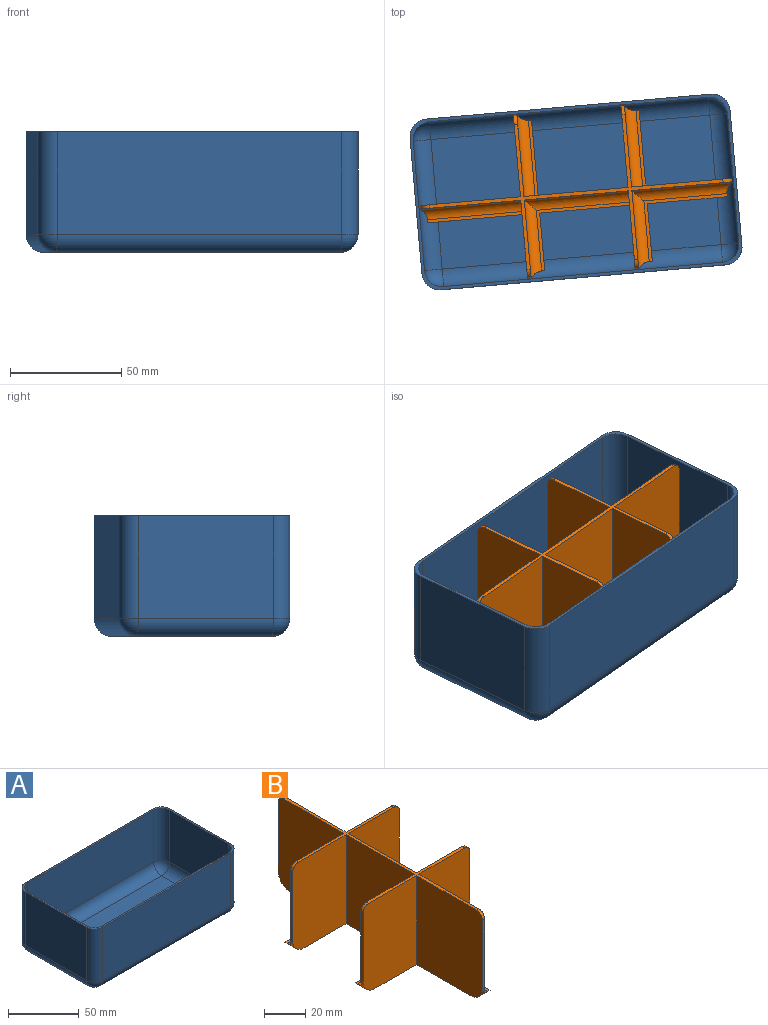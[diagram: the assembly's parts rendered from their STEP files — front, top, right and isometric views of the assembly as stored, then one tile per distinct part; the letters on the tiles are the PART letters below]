
ASSEMBLY  parts=2 mates=1
PART A: 35 faces, bbox 144.6x77.1x54.3 mm
  f0: plane 61.1x46.3mm, normal (1,0,0), area 2828.9mm2, adj f8,f13,f16,f26
  f1: plane 128.6x46.3mm, normal (0,1,0), area 5954.2mm2, adj f8,f13,f14,f22
  f2: plane 61.1x46.3mm, normal (-1,0,0), area 2828.9mm2, adj f8,f14,f15,f19
  f3: plane 58.5x45mm, normal (1,0,0), area 2632.5mm2, adj f8,f9,f12,f32
  f4: plane 126x45mm, normal (0,-1,0), area 5670mm2, adj f8,f9,f10,f28
  f5: plane 58.5x45mm, normal (-1,0,0), area 2632.5mm2, adj f8,f10,f11,f29
  f6: plane 126x45mm, normal (0,1,0), area 5670mm2, adj f8,f11,f12,f33
  f7: plane 128.6x46.3mm, normal (0,-1,0), area 5954.2mm2, adj f8,f15,f16,f23
  f8: plane 144.6x77.1mm, normal (0,0,1), area 569.7mm2, adj f0,f1,f2,f3,f4,f5,f6,f7
  f9: cylinder r=8mm len=45mm, axis (0,0,-1), area 565.5mm2, adj f3,f4,f8,f30
  f10: cylinder r=8mm len=45mm, axis (0,0,1), area 565.5mm2, adj f4,f5,f8,f27
  f11: cylinder r=8mm len=45mm, axis (0,0,-1), area 565.5mm2, adj f5,f6,f8,f31
  f12: cylinder r=8mm len=45mm, axis (0,0,1), area 565.5mm2, adj f3,f6,f8,f34
  f13: cylinder r=8mm len=46.3mm, axis (0,0,-1), area 581.8mm2, adj f0,f1,f8,f24
  f14: cylinder r=8mm len=46.3mm, axis (0,0,1), area 581.8mm2, adj f1,f2,f8,f20
  f15: cylinder r=8mm len=46.3mm, axis (0,0,-1), area 581.8mm2, adj f2,f7,f8,f21
  f16: cylinder r=8mm len=46.3mm, axis (0,0,1), area 581.8mm2, adj f0,f7,f8,f25
  f17: plane 126x58.5mm, normal (0,0,1), area 7371mm2, adj f28,f29,f32,f33
  f18: plane 128.6x61.1mm, normal (0,0,-1), area 7857.5mm2, adj f19,f22,f23,f26
  f19: cylinder r=8mm len=61.1mm, axis (0,-1,0), area 767.8mm2, adj f2,f18,f20,f21
  f20: sphere r=8mm, area 100.5mm2, adj f14,f19,f22
  f21: sphere r=8mm, area 100.5mm2, adj f15,f19,f23
  f22: cylinder r=8mm len=128.6mm, axis (-1,0,0), area 1616mm2, adj f1,f18,f20,f24
  f23: cylinder r=8mm len=128.6mm, axis (1,0,0), area 1616mm2, adj f7,f18,f21,f25
  f24: sphere r=8mm, area 100.5mm2, adj f13,f22,f26
  f25: sphere r=8mm, area 100.5mm2, adj f16,f23,f26
  f26: cylinder r=8mm len=61.1mm, axis (0,1,0), area 767.8mm2, adj f0,f18,f24,f25
  f27: sphere r=8mm, area 100.5mm2, adj f10,f28,f29
  f28: cylinder r=8mm len=126mm, axis (1,0,0), area 1583.4mm2, adj f4,f17,f27,f30
  f29: cylinder r=8mm len=58.5mm, axis (0,-1,0), area 735.1mm2, adj f5,f17,f27,f31
  f30: sphere r=8mm, area 100.5mm2, adj f9,f28,f32
  f31: sphere r=8mm, area 100.5mm2, adj f11,f29,f33
  f32: cylinder r=8mm len=58.5mm, axis (0,1,0), area 735.1mm2, adj f3,f17,f30,f34
  f33: cylinder r=8mm len=126mm, axis (-1,0,0), area 1583.4mm2, adj f6,f17,f31,f34
  f34: sphere r=8mm, area 100.5mm2, adj f12,f32,f33
PART B: 53 faces, bbox 73.5x140.7x53 mm
  f0: plane 40.6x2mm, normal (1,0,0), area 81.2mm2, adj f8,f11,f23,f30
  f1: plane 42.54x2mm, normal (1,0,0), area 81.8mm2, adj f2,f11,f32,f39
  f2: plane 42.54x1.4mm, normal (0,0,1), area 59.6mm2, adj f1,f32,f39,f40
  f3: plane 47x46mm, normal (1,0,0), area 2162mm2, adj f13,f23,f31,f43
  f4: plane 46x45.25mm, normal (1,0,0), area 2078mm2, adj f13,f14,f32,f39,f40,f52
  f5: plane 53x47mm, normal (-1,0,0), area 2472.8mm2, adj f11,f13,f20,f26,f27,f28,f45
  f6: plane 53x45.25mm, normal (-1,0,0), area 2381.1mm2, adj f11,f13,f14,f29,f39,f52
  f7: plane 36.14x2mm, normal (1,0,0), area 69mm2, adj f11,f12,f21,f38
  f8: plane 42x27.44mm, normal (0,0,1), area 95.3mm2, adj f0,f23,f30,f35,f43,f44
  f9: plane 46x45.25mm, normal (1,0,0), area 2078mm2, adj f13,f15,f22,f38,f41,f51
  f10: plane 53x45.25mm, normal (-1,0,0), area 2362.9mm2, adj f11,f13,f15,f17,f18,f19,f38,f46
  f11: plane 124.7x57.5mm, normal (0,0,-1), area 1789.6mm2, adj f0,f1,f5,f6,f7,f10,f19,f20
  f12: plane 37.54x27.44mm, normal (0,0,1), area 89mm2, adj f7,f21,f37,f38,f41,f42
  f13: plane 132.7x65.5mm, normal (0,0,1), area 416.8mm2, adj f3,f4,f5,f6,f9,f10,f17,f20
  f14: plane 41x1.6mm, normal (0,-1,0), area 65.6mm2, adj f4,f6,f39,f52
  f15: plane 41x1.6mm, normal (0,1,0), area 65.6mm2, adj f9,f10,f38,f51
  f16: plane 41x1.6mm, normal (-1,0,0), area 65.6mm2, adj f17,f20,f36,f49
  f17: plane 46x36.75mm, normal (0,1,0), area 1687mm2, adj f10,f13,f16,f36,f46,f49
  f18: plane 34.04x1.4mm, normal (0,0,1), area 47.7mm2, adj f10,f19,f36,f46
  f19: plane 34.04x2mm, normal (0,1,0), area 64.8mm2, adj f10,f11,f18,f36
  f20: plane 53x36.75mm, normal (0,-1,0), area 1930.6mm2, adj f5,f11,f13,f16,f36,f49
  f21: plane 26.04x2mm, normal (0,1,0), area 48.8mm2, adj f7,f11,f12,f37
  f22: plane 46x35.15mm, normal (0,1,0), area 1613.4mm2, adj f9,f13,f24,f37,f42,f50
  f23: plane 53x35.15mm, normal (0,-1,0), area 1827.6mm2, adj f0,f3,f8,f11,f13,f24,f37,f43
  f24: plane 41x1.6mm, normal (1,0,0), area 65.6mm2, adj f22,f23,f37,f50
  f25: plane 41x1.6mm, normal (-1,0,0), area 65.6mm2, adj f26,f29,f34,f47
  f26: plane 46x36.75mm, normal (0,1,0), area 1687mm2, adj f5,f13,f25,f34,f45,f47
  f27: plane 34.04x1.4mm, normal (0,0,1), area 47.7mm2, adj f5,f28,f34,f45
  f28: plane 34.04x2mm, normal (0,1,0), area 64.8mm2, adj f5,f11,f27,f34
  f29: plane 53x36.75mm, normal (0,-1,0), area 1930.6mm2, adj f6,f11,f13,f25,f34,f47
  f30: plane 26.04x2mm, normal (0,1,0), area 48.8mm2, adj f0,f8,f11,f35
  f31: plane 46x35.15mm, normal (0,1,0), area 1613.4mm2, adj f3,f13,f33,f35,f44,f48
  f32: plane 53x35.15mm, normal (0,-1,0), area 1827.6mm2, adj f1,f2,f4,f11,f13,f33,f35,f40
  f33: plane 41x1.6mm, normal (1,0,0), area 65.6mm2, adj f31,f32,f35,f48
  f34: cylinder r=8mm len=8mm, axis (0,1,0), area 64.1mm2, adj f11,f25,f26,f27,f28,f29,f45
  f35: cylinder r=8mm len=8mm, axis (0,-1,0), area 64.1mm2, adj f8,f11,f30,f31,f32,f33,f44
  f36: cylinder r=8mm len=8mm, axis (0,1,0), area 64.1mm2, adj f11,f16,f17,f18,f19,f20,f46
  f37: cylinder r=8mm len=8mm, axis (0,-1,0), area 64.1mm2, adj f11,f12,f21,f22,f23,f24,f42
  f38: cylinder r=8mm len=8mm, axis (1,0,0), area 64.1mm2, adj f7,f9,f10,f11,f12,f15,f41
  f39: cylinder r=8mm len=8mm, axis (-1,0,0), area 64.1mm2, adj f1,f2,f4,f6,f11,f14,f40
  f40: cylinder r=5mm len=45.19mm, axis (0,1,0), area 344.3mm2, adj f2,f4,f32,f39
  f41: cylinder r=5mm len=45.19mm, axis (0,1,0), area 330mm2, adj f9,f12,f38,f42
  f42: cylinder r=5mm len=35.09mm, axis (-1,0,0), area 250.7mm2, adj f12,f22,f37,f41
  f43: cylinder r=5mm len=47mm, axis (0,1,0), area 354.9mm2, adj f3,f8,f23,f44
  f44: cylinder r=5mm len=35.09mm, axis (-1,0,0), area 250.7mm2, adj f8,f31,f35,f43
  f45: cylinder r=5mm len=36.69mm, axis (-1,0,0), area 277.5mm2, adj f5,f26,f27,f34
  f46: cylinder r=5mm len=36.69mm, axis (-1,0,0), area 277.5mm2, adj f10,f17,f18,f36
  f47: cylinder r=4mm len=4mm, axis (0,-1,0), area 10.1mm2, adj f13,f25,f26,f29
  f48: cylinder r=4mm len=4mm, axis (0,1,0), area 10.1mm2, adj f13,f31,f32,f33
  f49: cylinder r=4mm len=4mm, axis (0,-1,0), area 10.1mm2, adj f13,f16,f17,f20
  f50: cylinder r=4mm len=4mm, axis (0,1,0), area 10.1mm2, adj f13,f22,f23,f24
  f51: cylinder r=4mm len=4mm, axis (-1,0,0), area 10.1mm2, adj f9,f10,f13,f15
  f52: cylinder r=4mm len=4mm, axis (1,0,0), area 10.1mm2, adj f4,f6,f13,f14
PLACE A rot(axis=(0,0,1),5deg) t=(-0.85,4.73,-15.91)mm
PLACE B rot(axis=(0,0,-1),85deg) t=(-0.85,4.73,-15.91)mm
MATE revolute B.f11 <-> A.f17  axis (0,0,1) through (-0.85,4.73,-15.91)mm
